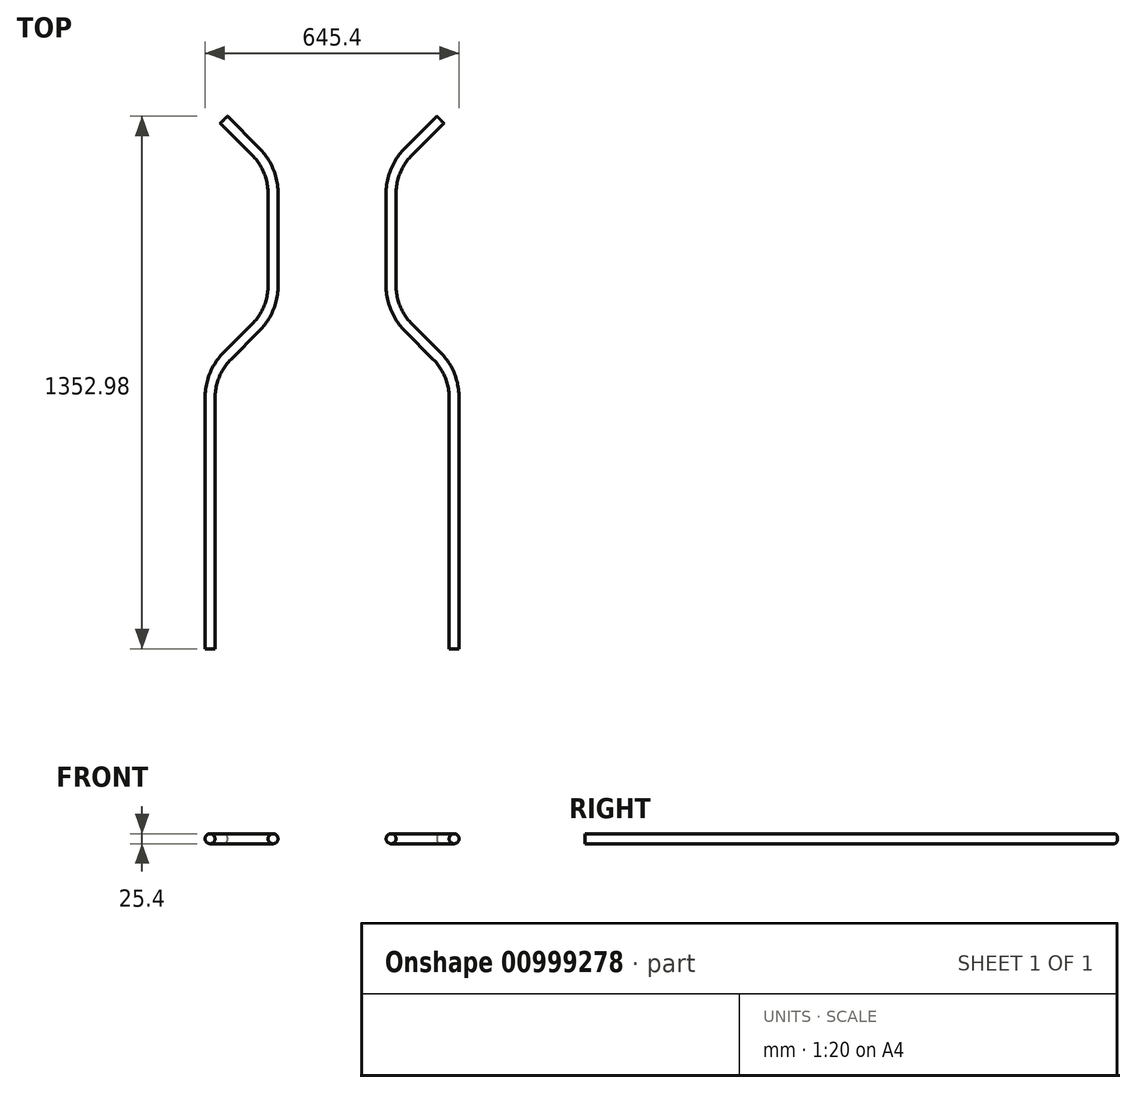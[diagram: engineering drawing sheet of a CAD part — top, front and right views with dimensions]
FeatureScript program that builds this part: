
annotation { "Feature Type Name" : "Feature", "Feature Type Description" : "" }
export const myFeature = defineFeature(function(context is Context, id is Id, definition is map)
    precondition{}
    {
        {
            var Q0;
            Q0=qCreatedBy(makeId("Top.planeOp"),FACE);
            var sketch = newSketch(context, id + "F0", { "sketchPlane" : qUnion([Q0])});
            skLineSegment(sketch, "E0", {"start": v(-310, 0) * mm, "end": v(-310, 637.87) * mm});
            skLineSegment(sketch, "E1", {"start": v(310, 0) * mm, "end": v(310, 637.87) * mm});
            skLineSegment(sketch, "E2", {"start": v(-266.07, 743.93) * mm, "end": v(-193.93, 816.07) * mm});
            skLineSegment(sketch, "E3", {"start": v(-150, 922.13) * mm, "end": v(-150, 1156.87) * mm});
            skLineSegment(sketch, "E4", {"start": v(-193.93, 1262.93) * mm, "end": v(-275, 1344) * mm});
            skLineSegment(sketch, "E5", {"start": v(266.07, 743.93) * mm, "end": v(193.93, 816.07) * mm});
            skLineSegment(sketch, "E6", {"start": v(150, 922.13) * mm, "end": v(150, 1156.87) * mm});
            skLineSegment(sketch, "E7", {"start": v(275, 1344) * mm, "end": v(193.93, 1262.93) * mm});
            skLineSegment(sketch, "E8", {"start": v(-340, 1240) * mm, "end": v(-190, 1480) * mm});
            skLineSegment(sketch, "E9", {"start": v(-190, 1480) * mm, "end": v(190, 1480) * mm});
            skLineSegment(sketch, "E10", {"start": v(190, 1480) * mm, "end": v(340, 1240) * mm});
            skLineSegment(sketch, "E11", {"start": v(0, 0) * mm, "end": v(0, 1480) * mm});
            skPoint(sketch, "E12", {"position": v(-230, 780) * mm});
            skPoint(sketch, "E13", {"position": v(230, 780) * mm});
            skPoint(sketch, "E14", {"position": v(-310, 400) * mm});
            skPoint(sketch, "E15", {"position": v(310, 400) * mm});
            skPoint(sketch, "E16", {"position": v(150, 900) * mm});
            skPoint(sketch, "E17", {"position": v(-150, 900) * mm});
            skPoint(sketch, "E18", {"position": v(-171, 1240) * mm});
            skPoint(sketch, "E19", {"position": v(171, 1240) * mm});
            skPoint(sketch, "E20", {"position": v(-310, 200) * mm});
            skPoint(sketch, "E21", {"position": v(310, 200) * mm});
            skPoint(sketch, "E22.visualSharp", {"position": v(-150, 1219) * mm});
            skArc(sketch, "E22.filletArc", {"start": v(-150, 1156.87) * mm, "mid": v(-161.42, 1214.27) * mm, "end": v(-193.93, 1262.93) * mm});
            skPoint(sketch, "E23.visualSharp", {"position": v(-150, 860) * mm});
            skArc(sketch, "E23.filletArc", {"start": v(-193.93, 816.07) * mm, "mid": v(-161.42, 864.73) * mm, "end": v(-150, 922.13) * mm});
            skPoint(sketch, "E24.visualSharp", {"position": v(-310, 700) * mm});
            skArc(sketch, "E24.filletArc", {"start": v(-266.07, 743.93) * mm, "mid": v(-298.58, 695.27) * mm, "end": v(-310, 637.87) * mm});
            skPoint(sketch, "E25.visualSharp", {"position": v(150, 1219) * mm});
            skArc(sketch, "E25.filletArc", {"start": v(193.93, 1262.93) * mm, "mid": v(161.42, 1214.27) * mm, "end": v(150, 1156.87) * mm});
            skPoint(sketch, "E26.visualSharp", {"position": v(150, 860) * mm});
            skArc(sketch, "E26.filletArc", {"start": v(150, 922.13) * mm, "mid": v(161.42, 864.73) * mm, "end": v(193.93, 816.07) * mm});
            skPoint(sketch, "E27.visualSharp", {"position": v(310, 700) * mm});
            skArc(sketch, "E27.filletArc", {"start": v(310, 637.87) * mm, "mid": v(298.58, 695.27) * mm, "end": v(266.07, 743.93) * mm});
            skSolve(sketch);
        }
        {
            var Q0;
            Q0=sQuery(id+"F0.wireOp",VERTEX,"E0.start");
            var Q1;
            Q1=sQuery(id+"F0.wireOp",EDGE,"E0");
            cPlane(context, id + "F1", {"entities" : qUnion([Q0, Q1]), "cplaneType" : CPlaneType.CURVE_POINT, "offset" : 25 * mm, "width" : 150 * mm, "height" : 150 * mm});
        }
        {
            var Q0;
            Q0=qCreatedBy(id+"F1.planeOp",FACE);
            var sketch = newSketch(context, id + "F2", { "sketchPlane" : qUnion([Q0])});
            skCircle(sketch, "E28", {"center": v(310, 0) * mm, "radius": 12.7 * mm});
            skSolve(sketch);
        }
        {
            var Q0;
            Q0=makeQuery(id+"F2.imprint","IMPRINT",FACE,{"disambiguationData":[TD([[makeQuery(id+"F2.imprint","IMPRINT",EDGE,{"derivedFrom":sQuery(id+"F2.wireOp",EDGE,"E28")}),1.0]])]});
            var Q1;
            Q1=sQuery(id+"F0.wireOp",EDGE,"E0");
            var Q2;
            Q2=sQuery(id+"F0.wireOp",EDGE,"E24.filletArc");
            var Q3;
            Q3=sQuery(id+"F0.wireOp",EDGE,"E2");
            var Q4;
            Q4=sQuery(id+"F0.wireOp",EDGE,"E23.filletArc");
            var Q5;
            Q5=sQuery(id+"F0.wireOp",EDGE,"E3");
            var Q6;
            Q6=sQuery(id+"F0.wireOp",EDGE,"E22.filletArc");
            var Q7;
            Q7=sQuery(id+"F0.wireOp",EDGE,"E4");
            sweep(context, id + "F3", {"profiles" : qUnion([Q0]), "path" : qUnion([Q1, Q2, Q3, Q4, Q5, Q6, Q7])});
        }
        {
            var Q0;
            Q0=makeQuery(id+"F3.opSweep","SWEPT_BODY",BODY,{"disambiguationData":[OSD([sQuery(id+"F0.wireOp",EDGE,"E4"),sQuery(id+"F2.wireOp",EDGE,"E28")])]});
            var Q1;
            Q1=qCreatedBy(makeId("Right.planeOp"),FACE);
            mirror(context, id + "F4", {"entities" : qUnion([Q0]), "mirrorPlane" : qUnion([Q1])});
        }
    });
